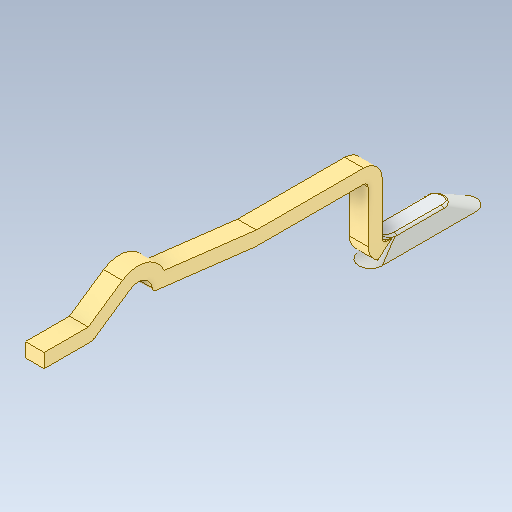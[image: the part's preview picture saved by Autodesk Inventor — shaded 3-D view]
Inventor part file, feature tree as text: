
AUTODESK INVENTOR PART (.ipt)
format: ipt  version: 2020.1 (Build 241239000, 239)  size: 168,960 bytes
history: native  units: mm
features: fillet x1
ambient origin geometry x8: Origin, YZ Plane, XZ Plane, XY Plane, X Axis, Y Axis, Z Axis, Center Point
bodies: Solid1 (feature_tree)
feature tree (1):
  fillet  "Fillet2"  [1 undecoded]
note: 1 required parameter value undecoded (feature->parameter linkage not recoverable at this tier; creation-order binding heuristic only, values carry confidence <= 0.55)
